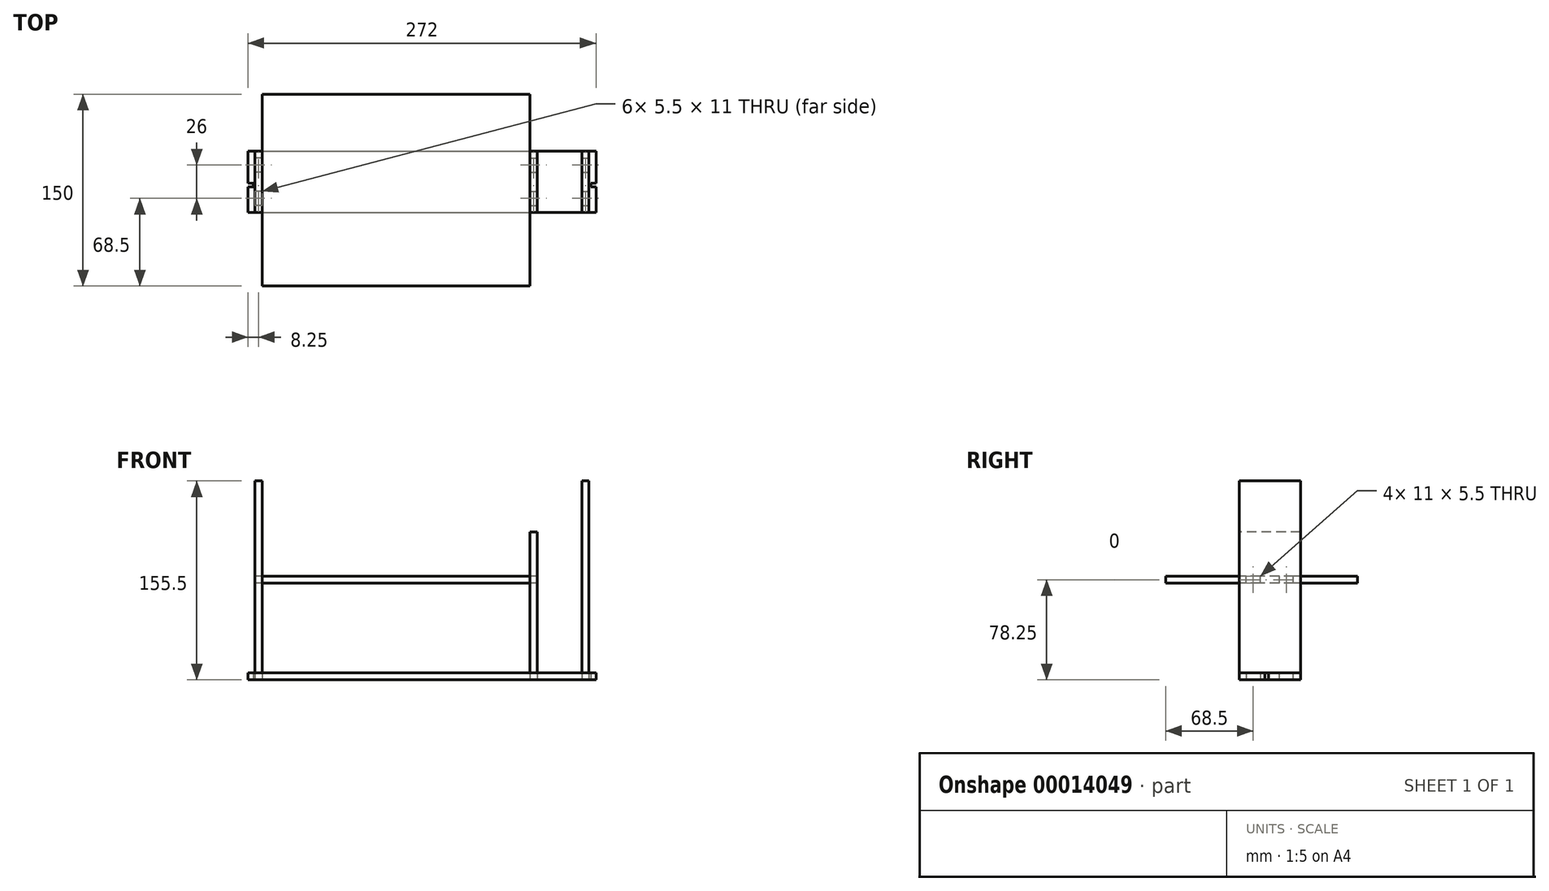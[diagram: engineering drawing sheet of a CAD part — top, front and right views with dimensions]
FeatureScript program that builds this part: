
annotation { "Feature Type Name" : "Feature", "Feature Type Description" : "" }
export const myFeature = defineFeature(function(context is Context, id is Id, definition is map)
    precondition{}
    {
        {
            var Q0;
            Q0=qCreatedBy(makeId("Top.planeOp"),FACE);
            var sketch = newSketch(context, id + "F0", { "sketchPlane" : qUnion([Q0])});
            skLineSegment(sketch, "E0.bottom", {"start": v(-272, -25) * mm, "end": v(0, -25) * mm});
            skLineSegment(sketch, "E0.top", {"start": v(-272, 0) * mm, "end": v(0, 0) * mm});
            skLineSegment(sketch, "E0.left", {"start": v(-272, -25) * mm, "end": v(-272, 0) * mm});
            skLineSegment(sketch, "E0.right", {"start": v(0, -25) * mm, "end": v(0, 0) * mm});
            skLineSegment(sketch, "E1.bottom", {"start": v(-268, -25) * mm, "end": v(-4, -25) * mm});
            skLineSegment(sketch, "E1.top", {"start": v(-268, -28) * mm, "end": v(-4, -28) * mm});
            skLineSegment(sketch, "E1.left", {"start": v(-268, -25) * mm, "end": v(-268, -28) * mm});
            skLineSegment(sketch, "E1.right", {"start": v(-4, -25) * mm, "end": v(-4, -28) * mm});
            skLineSegment(sketch, "E2.bottom", {"start": v(-272, -28) * mm, "end": v(0, -28) * mm});
            skLineSegment(sketch, "E2.top", {"start": v(-272, -48) * mm, "end": v(0, -48) * mm});
            skLineSegment(sketch, "E2.left", {"start": v(-272, -28) * mm, "end": v(-272, -48) * mm});
            skLineSegment(sketch, "E2.right", {"start": v(0, -28) * mm, "end": v(0, -48) * mm});
            skSolve(sketch);
        }
        {
            var Q0;
            Q0 = qSketchRegion(id + "F0", true);
            extrude(context, id + "F1", {"entities" : qUnion([Q0]), "depth" : 5.5 * mm});
        }
        {
            var Q0;
            Q0=makeQuery(id+"F1.opExtrude","CAP_FACE",FACE,{"disambiguationData":[OSD([sQuery(id+"F0.wireOp",EDGE,"E0.bottom"),sQuery(id+"F0.wireOp",EDGE,"E0.top"),sQuery(id+"F0.wireOp",EDGE,"E0.left"),sQuery(id+"F0.wireOp",EDGE,"E0.right"),sQuery(id+"F0.wireOp",EDGE,"E1.left"),sQuery(id+"F0.wireOp",EDGE,"E1.right"),sQuery(id+"F0.wireOp",EDGE,"E2.bottom"),sQuery(id+"F0.wireOp",EDGE,"E2.top"),sQuery(id+"F0.wireOp",EDGE,"E2.left"),sQuery(id+"F0.wireOp",EDGE,"E2.right")])],"isStart":false});
            var sketch = newSketch(context, id + "F2", { "sketchPlane" : qUnion([Q0])});
            skLineSegment(sketch, "E3.bottom", {"start": v(-266.5, -5.5) * mm, "end": v(-261, -5.5) * mm});
            skLineSegment(sketch, "E3.top", {"start": v(-266.5, -16.5) * mm, "end": v(-261, -16.5) * mm});
            skLineSegment(sketch, "E3.left", {"start": v(-266.5, -5.5) * mm, "end": v(-266.5, -16.5) * mm});
            skLineSegment(sketch, "E3.right", {"start": v(-261, -5.5) * mm, "end": v(-261, -16.5) * mm});
            skLineSegment(sketch, "E4.bottom", {"start": v(-266.5, -31.5) * mm, "end": v(-261, -31.5) * mm});
            skLineSegment(sketch, "E4.top", {"start": v(-266.5, -42.5) * mm, "end": v(-261, -42.5) * mm});
            skLineSegment(sketch, "E4.left", {"start": v(-266.5, -31.5) * mm, "end": v(-266.5, -42.5) * mm});
            skLineSegment(sketch, "E4.right", {"start": v(-261, -31.5) * mm, "end": v(-261, -42.5) * mm});
            skLineSegment(sketch, "E5.bottom", {"start": v(-11, -5.5) * mm, "end": v(-5.5, -5.5) * mm});
            skLineSegment(sketch, "E5.top", {"start": v(-11, -16.5) * mm, "end": v(-5.5, -16.5) * mm});
            skLineSegment(sketch, "E5.left", {"start": v(-11, -5.5) * mm, "end": v(-11, -16.5) * mm});
            skLineSegment(sketch, "E5.right", {"start": v(-5.5, -5.5) * mm, "end": v(-5.5, -16.5) * mm});
            skLineSegment(sketch, "E6.bottom", {"start": v(-11, -31.5) * mm, "end": v(-5.5, -31.5) * mm});
            skLineSegment(sketch, "E6.top", {"start": v(-11, -42.5) * mm, "end": v(-5.5, -42.5) * mm});
            skLineSegment(sketch, "E6.left", {"start": v(-11, -31.5) * mm, "end": v(-11, -42.5) * mm});
            skLineSegment(sketch, "E6.right", {"start": v(-5.5, -31.5) * mm, "end": v(-5.5, -42.5) * mm});
            skLineSegment(sketch, "E7.bottom", {"start": v(-46, -5.5) * mm, "end": v(-51.5, -5.5) * mm});
            skLineSegment(sketch, "E7.top", {"start": v(-46, -16.5) * mm, "end": v(-51.5, -16.5) * mm});
            skLineSegment(sketch, "E7.left", {"start": v(-46, -5.5) * mm, "end": v(-46, -16.5) * mm});
            skLineSegment(sketch, "E7.right", {"start": v(-51.5, -5.5) * mm, "end": v(-51.5, -16.5) * mm});
            skLineSegment(sketch, "E8.bottom", {"start": v(-46, -31.5) * mm, "end": v(-51.5, -31.5) * mm});
            skLineSegment(sketch, "E8.top", {"start": v(-46, -42.5) * mm, "end": v(-51.5, -42.5) * mm});
            skLineSegment(sketch, "E8.left", {"start": v(-46, -31.5) * mm, "end": v(-46, -42.5) * mm});
            skLineSegment(sketch, "E8.right", {"start": v(-51.5, -31.5) * mm, "end": v(-51.5, -42.5) * mm});
            skSolve(sketch);
        }
        {
            var Q0;
            Q0 = qSketchRegion(id + "F2", true);
            extrude(context, id + "F3", {"entities" : qUnion([Q0]), "operationType" : NewBodyOperationType.REMOVE, "oppositeDirection" : true, "depth" : 5.5 * mm});
        }
        {
            var Q0;
            Q0=makeQuery(id+"F3.boolean.opBoolean","COPY",FACE,{"derivedFrom":makeQuery(id+"F3.opExtrude","SWEPT_FACE",FACE,{"disambiguationData":[OSD([sQuery(id+"F2.wireOp",EDGE,"E5.right")])]})});
            var sketch = newSketch(context, id + "F4", { "sketchPlane" : qUnion([Q0])});
            skLineSegment(sketch, "E9.bottom", {"start": v(0, 5.5) * mm, "end": v(48, 5.5) * mm});
            skLineSegment(sketch, "E9.top", {"start": v(0, 155.5) * mm, "end": v(48, 155.5) * mm});
            skLineSegment(sketch, "E9.left", {"start": v(0, 5.5) * mm, "end": v(0, 155.5) * mm});
            skLineSegment(sketch, "E9.right", {"start": v(48, 5.5) * mm, "end": v(48, 155.5) * mm});
            skLineSegment(sketch, "E10.bottom", {"start": v(5.5, 5.5) * mm, "end": v(16.5, 5.5) * mm});
            skLineSegment(sketch, "E10.top", {"start": v(5.5, 0) * mm, "end": v(16.5, 0) * mm});
            skLineSegment(sketch, "E10.left", {"start": v(5.5, 5.5) * mm, "end": v(5.5, 0) * mm});
            skLineSegment(sketch, "E10.right", {"start": v(16.5, 5.5) * mm, "end": v(16.5, 0) * mm});
            skLineSegment(sketch, "E11.bottom", {"start": v(31.5, 5.5) * mm, "end": v(42.5, 5.5) * mm});
            skLineSegment(sketch, "E11.top", {"start": v(31.5, 0) * mm, "end": v(42.5, 0) * mm});
            skLineSegment(sketch, "E11.left", {"start": v(31.5, 5.5) * mm, "end": v(31.5, 0) * mm});
            skLineSegment(sketch, "E11.right", {"start": v(42.5, 5.5) * mm, "end": v(42.5, 0) * mm});
            skSolve(sketch);
        }
        {
            var Q0;
            Q0 = qSketchRegion(id + "F4", true);
            extrude(context, id + "F5", {"entities" : qUnion([Q0]), "depth" : 5.5 * mm});
        }
        {
            var Q0;
            Q0=makeQuery(id+"F3.boolean.opBoolean","COPY",FACE,{"derivedFrom":makeQuery(id+"F3.opExtrude","SWEPT_FACE",FACE,{"disambiguationData":[OSD([sQuery(id+"F2.wireOp",EDGE,"E3.right")])]})});
            var sketch = newSketch(context, id + "F6", { "sketchPlane" : qUnion([Q0])});
            skLineSegment(sketch, "E12.bottom", {"start": v(0, 5.5) * mm, "end": v(48, 5.5) * mm});
            skLineSegment(sketch, "E12.top", {"start": v(0, 155.5) * mm, "end": v(48, 155.5) * mm});
            skLineSegment(sketch, "E12.left", {"start": v(0, 5.5) * mm, "end": v(0, 155.5) * mm});
            skLineSegment(sketch, "E12.right", {"start": v(48, 5.5) * mm, "end": v(48, 155.5) * mm});
            skLineSegment(sketch, "E13.bottom", {"start": v(5.5, 5.5) * mm, "end": v(16.5, 5.5) * mm});
            skLineSegment(sketch, "E13.top", {"start": v(5.5, 0) * mm, "end": v(16.5, 0) * mm});
            skLineSegment(sketch, "E13.left", {"start": v(5.5, 5.5) * mm, "end": v(5.5, 0) * mm});
            skLineSegment(sketch, "E13.right", {"start": v(16.5, 5.5) * mm, "end": v(16.5, 0) * mm});
            skLineSegment(sketch, "E14.bottom", {"start": v(31.5, 5.5) * mm, "end": v(42.5, 5.5) * mm});
            skLineSegment(sketch, "E14.top", {"start": v(31.5, 0) * mm, "end": v(42.5, 0) * mm});
            skLineSegment(sketch, "E14.left", {"start": v(31.5, 5.5) * mm, "end": v(31.5, 0) * mm});
            skLineSegment(sketch, "E14.right", {"start": v(42.5, 5.5) * mm, "end": v(42.5, 0) * mm});
            skSolve(sketch);
        }
        {
            var Q0;
            Q0 = qSketchRegion(id + "F6", true);
            extrude(context, id + "F7", {"entities" : qUnion([Q0]), "depth" : 5.5 * mm});
        }
        {
            var Q0;
            Q0=makeQuery(id+"F3.boolean.opBoolean","COPY",FACE,{"derivedFrom":makeQuery(id+"F3.opExtrude","SWEPT_FACE",FACE,{"disambiguationData":[OSD([sQuery(id+"F2.wireOp",EDGE,"E7.left")])]})});
            var sketch = newSketch(context, id + "F8", { "sketchPlane" : qUnion([Q0])});
            skLineSegment(sketch, "E15.bottom", {"start": v(0, 5.5) * mm, "end": v(48, 5.5) * mm});
            skLineSegment(sketch, "E15.top", {"start": v(0, 115.5) * mm, "end": v(48, 115.5) * mm});
            skLineSegment(sketch, "E15.left", {"start": v(0, 5.5) * mm, "end": v(0, 115.5) * mm});
            skLineSegment(sketch, "E15.right", {"start": v(48, 5.5) * mm, "end": v(48, 115.5) * mm});
            skLineSegment(sketch, "E16.bottom", {"start": v(31.5, 5.5) * mm, "end": v(42.5, 5.5) * mm});
            skLineSegment(sketch, "E16.top", {"start": v(31.5, 0) * mm, "end": v(42.5, 0) * mm});
            skLineSegment(sketch, "E16.left", {"start": v(31.5, 5.5) * mm, "end": v(31.5, 0) * mm});
            skLineSegment(sketch, "E16.right", {"start": v(42.5, 5.5) * mm, "end": v(42.5, 0) * mm});
            skLineSegment(sketch, "E17.bottom", {"start": v(5.5, 5.5) * mm, "end": v(16.5, 5.5) * mm});
            skLineSegment(sketch, "E17.top", {"start": v(5.5, 0) * mm, "end": v(16.5, 0) * mm});
            skLineSegment(sketch, "E17.left", {"start": v(5.5, 5.5) * mm, "end": v(5.5, 0) * mm});
            skLineSegment(sketch, "E17.right", {"start": v(16.5, 5.5) * mm, "end": v(16.5, 0) * mm});
            skSolve(sketch);
        }
        {
            var Q0;
            Q0 = qSketchRegion(id + "F8", true);
            extrude(context, id + "F9", {"entities" : qUnion([Q0]), "depth" : 5.5 * mm});
        }
        {
            var Q0;
            Q0=makeQuery(id+"F9.opExtrude","CAP_FACE",FACE,{"disambiguationData":[OSD([sQuery(id+"F8.wireOp",EDGE,"E15.bottom"),sQuery(id+"F8.wireOp",EDGE,"E15.top"),sQuery(id+"F8.wireOp",EDGE,"E15.left"),sQuery(id+"F8.wireOp",EDGE,"E15.right"),sQuery(id+"F8.wireOp",EDGE,"E16.top"),sQuery(id+"F8.wireOp",EDGE,"E16.left"),sQuery(id+"F8.wireOp",EDGE,"E16.right"),sQuery(id+"F8.wireOp",EDGE,"E17.top"),sQuery(id+"F8.wireOp",EDGE,"E17.left"),sQuery(id+"F8.wireOp",EDGE,"E17.right")])],"isStart":false});
            var sketch = newSketch(context, id + "F10", { "sketchPlane" : qUnion([Q0])});
            skLineSegment(sketch, "E18.bottom", {"start": v(5.5, 75.5) * mm, "end": v(16.5, 75.5) * mm});
            skLineSegment(sketch, "E18.top", {"start": v(5.5, 81) * mm, "end": v(16.5, 81) * mm});
            skLineSegment(sketch, "E18.left", {"start": v(5.5, 75.5) * mm, "end": v(5.5, 81) * mm});
            skLineSegment(sketch, "E18.right", {"start": v(16.5, 75.5) * mm, "end": v(16.5, 81) * mm});
            skLineSegment(sketch, "E19.bottom", {"start": v(31.5, 75.5) * mm, "end": v(42.5, 75.5) * mm});
            skLineSegment(sketch, "E19.top", {"start": v(31.5, 81) * mm, "end": v(42.5, 81) * mm});
            skLineSegment(sketch, "E19.left", {"start": v(31.5, 75.5) * mm, "end": v(31.5, 81) * mm});
            skLineSegment(sketch, "E19.right", {"start": v(42.5, 75.5) * mm, "end": v(42.5, 81) * mm});
            skSolve(sketch);
        }
        {
            var Q0;
            Q0 = qSketchRegion(id + "F10", true);
            extrude(context, id + "F11", {"entities" : qUnion([Q0]), "operationType" : NewBodyOperationType.REMOVE, "oppositeDirection" : true, "depth" : 5.5 * mm});
        }
        {
            var Q0;
            Q0=makeQuery(id+"F7.opExtrude","CAP_FACE",FACE,{"disambiguationData":[OSD([sQuery(id+"F6.wireOp",EDGE,"E12.bottom"),sQuery(id+"F6.wireOp",EDGE,"E12.top"),sQuery(id+"F6.wireOp",EDGE,"E12.left"),sQuery(id+"F6.wireOp",EDGE,"E12.right"),sQuery(id+"F6.wireOp",EDGE,"E13.top"),sQuery(id+"F6.wireOp",EDGE,"E13.left"),sQuery(id+"F6.wireOp",EDGE,"E13.right"),sQuery(id+"F6.wireOp",EDGE,"E14.top"),sQuery(id+"F6.wireOp",EDGE,"E14.left"),sQuery(id+"F6.wireOp",EDGE,"E14.right")])],"isStart":true});
            var sketch = newSketch(context, id + "F12", { "sketchPlane" : qUnion([Q0])});
            skLineSegment(sketch, "E20.bottom", {"start": v(-42.5, 75.5) * mm, "end": v(-31.5, 75.5) * mm});
            skLineSegment(sketch, "E20.top", {"start": v(-42.5, 81) * mm, "end": v(-31.5, 81) * mm});
            skLineSegment(sketch, "E20.left", {"start": v(-42.5, 75.5) * mm, "end": v(-42.5, 81) * mm});
            skLineSegment(sketch, "E20.right", {"start": v(-31.5, 75.5) * mm, "end": v(-31.5, 81) * mm});
            skLineSegment(sketch, "E21.bottom", {"start": v(-16.5, 75.5) * mm, "end": v(-5.5, 75.5) * mm});
            skLineSegment(sketch, "E21.top", {"start": v(-16.5, 81) * mm, "end": v(-5.5, 81) * mm});
            skLineSegment(sketch, "E21.left", {"start": v(-16.5, 75.5) * mm, "end": v(-16.5, 81) * mm});
            skLineSegment(sketch, "E21.right", {"start": v(-5.5, 75.5) * mm, "end": v(-5.5, 81) * mm});
            skSolve(sketch);
        }
        {
            var Q0;
            Q0 = qSketchRegion(id + "F12", true);
            extrude(context, id + "F13", {"entities" : qUnion([Q0]), "operationType" : NewBodyOperationType.REMOVE, "oppositeDirection" : true, "depth" : 5.5 * mm});
        }
        {
            var Q0;
            Q0=makeQuery(id+"F11.boolean.opBoolean","COPY",FACE,{"derivedFrom":makeQuery(id+"F11.opExtrude","SWEPT_FACE",FACE,{"disambiguationData":[OSD([sQuery(id+"F10.wireOp",EDGE,"E18.bottom")])]})});
            var sketch = newSketch(context, id + "F14", { "sketchPlane" : qUnion([Q0])});
            skLineSegment(sketch, "E22.bottom", {"start": v(-51.5, 44.5) * mm, "end": v(-261, 44.5) * mm});
            skLineSegment(sketch, "E22.top", {"start": v(-51.5, -105.5) * mm, "end": v(-261, -105.5) * mm});
            skLineSegment(sketch, "E22.left", {"start": v(-51.5, 44.5) * mm, "end": v(-51.5, -105.5) * mm});
            skLineSegment(sketch, "E22.right", {"start": v(-261, 44.5) * mm, "end": v(-261, -105.5) * mm});
            skLineSegment(sketch, "E23.bottom", {"start": v(-51.5, -5.5) * mm, "end": v(-46, -5.5) * mm});
            skLineSegment(sketch, "E23.top", {"start": v(-51.5, -16.5) * mm, "end": v(-46, -16.5) * mm});
            skLineSegment(sketch, "E23.left", {"start": v(-51.5, -5.5) * mm, "end": v(-51.5, -16.5) * mm});
            skLineSegment(sketch, "E23.right", {"start": v(-46, -5.5) * mm, "end": v(-46, -16.5) * mm});
            skLineSegment(sketch, "E24.bottom", {"start": v(-51.5, -31.5) * mm, "end": v(-46, -31.5) * mm});
            skLineSegment(sketch, "E24.top", {"start": v(-51.5, -42.5) * mm, "end": v(-46, -42.5) * mm});
            skLineSegment(sketch, "E24.left", {"start": v(-51.5, -31.5) * mm, "end": v(-51.5, -42.5) * mm});
            skLineSegment(sketch, "E24.right", {"start": v(-46, -31.5) * mm, "end": v(-46, -42.5) * mm});
            skLineSegment(sketch, "E25.bottom", {"start": v(-261, -5.5) * mm, "end": v(-266.5, -5.5) * mm});
            skLineSegment(sketch, "E25.top", {"start": v(-261, -16.5) * mm, "end": v(-266.5, -16.5) * mm});
            skLineSegment(sketch, "E25.left", {"start": v(-261, -5.5) * mm, "end": v(-261, -16.5) * mm});
            skLineSegment(sketch, "E25.right", {"start": v(-266.5, -5.5) * mm, "end": v(-266.5, -16.5) * mm});
            skLineSegment(sketch, "E26.bottom", {"start": v(-261, -31.5) * mm, "end": v(-266.5, -31.5) * mm});
            skLineSegment(sketch, "E26.top", {"start": v(-261, -42.5) * mm, "end": v(-266.5, -42.5) * mm});
            skLineSegment(sketch, "E26.left", {"start": v(-261, -31.5) * mm, "end": v(-261, -42.5) * mm});
            skLineSegment(sketch, "E26.right", {"start": v(-266.5, -31.5) * mm, "end": v(-266.5, -42.5) * mm});
            skSolve(sketch);
        }
        {
            var Q0;
            Q0 = qSketchRegion(id + "F14", true);
            extrude(context, id + "F15", {"entities" : qUnion([Q0]), "depth" : 5.5 * mm});
        }
    });
